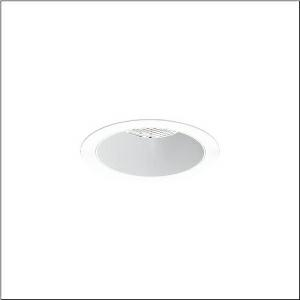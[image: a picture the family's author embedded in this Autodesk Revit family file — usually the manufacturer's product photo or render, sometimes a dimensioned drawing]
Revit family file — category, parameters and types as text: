
# Revit family: lunis_21_l_51db18md91c
name_source: partatom
category: Lighting Fixtures
units: mm (PartAtom-declared; Revit-internal decimal feet)

## family parameters
Cut with Voids When Loaded = No
Host = Face
Light Source = No
Part Type = Normal
Room Calculation Point = No
Round Connector Dimension = Use Diameter
Shared = No

## types (1)
- --- (1 x LED, 3560 lm, 21.7 W, 6500K)
    Apparent Load = 22 VA
    CIE Flux Codes = 87 97 99 100 100
    Color Rendering = 80
    Color Temperature = 6500K
    Default Elevation = 1800 mm
    Description = Lunis 21,  L, downlight, light control with lens, of PMMA, anti glare with reflector, of PC, light emission: direct distribution, LED rated luminous flux: 2.160lm, light colour: 830/840/865, with terminal, 3-pole, mains connection: 220..240V, AC/DC, 0/50..60Hz, housing, round, of diecast aluminium, traffic white (RAL 9016), diameter: 165mm, clamping range: 1..40mm, protection rating (complete): IP20, protection rating (on room side): IP54, insulation class (complete): insulation class II (safety insulation), certification: CE, impact resistance: IK03, packaging unit: 1 piece
    Height = 0 mm  [stored 0 ft]
    Lamp = 1 x LED
    Lamp Light Flux = 3560 lm
    Lamp Power = 21.7 W
    Lamp count = 1
    Length = 165 mm
    Luminous efficacy = 164 lm/W
    Manufacturer = Siteco
    ModVariant = No
    Model = 51DB18MD91C
    Mounting Place = Ceiling
    Mounting Type = Recessed
    Number of Poles = 1
    OnlyDefault = Yes
    Power Factor = 1
    Product Name = Lunis 21 L
    Product group = downlight
    ProductGroupID = 400
    Protection Class = Protection class II
    Protection Degree = IP 20
    RLX_Detail_Level = 1
    RLX_Emergency_Light_Flux = 0 lm
    RLX_Emergency_Type = 0
    RLX_Emergency_Type_DB = No
    RlxData = <blob elided: 14805 chars, md5=db031439>
    Socket = socket
    Standby Power = 0 W
    System Light Flux = 3560 lm
    System Power = 22 W
    Type Comments = individual setting: colour temperature 6500K, luminous flux: 100 % | (OFF | ON | ON | ON) | 650 mA
    Type Image = l_1291155.jpg
    URL = http://relux.com
    VarID = @adj_019464
    Voltage = 0 V
    Weight = 0.00 kg
    Width = 0 mm  [stored 0 ft]

note: [stored X ft] marks values corroborated as IEEE doubles in the binary element streams (Revit-internal decimal feet)

## geometry (parser evidence)
native form markers: Sweep x10
no freeform markers — native parametric forms only
